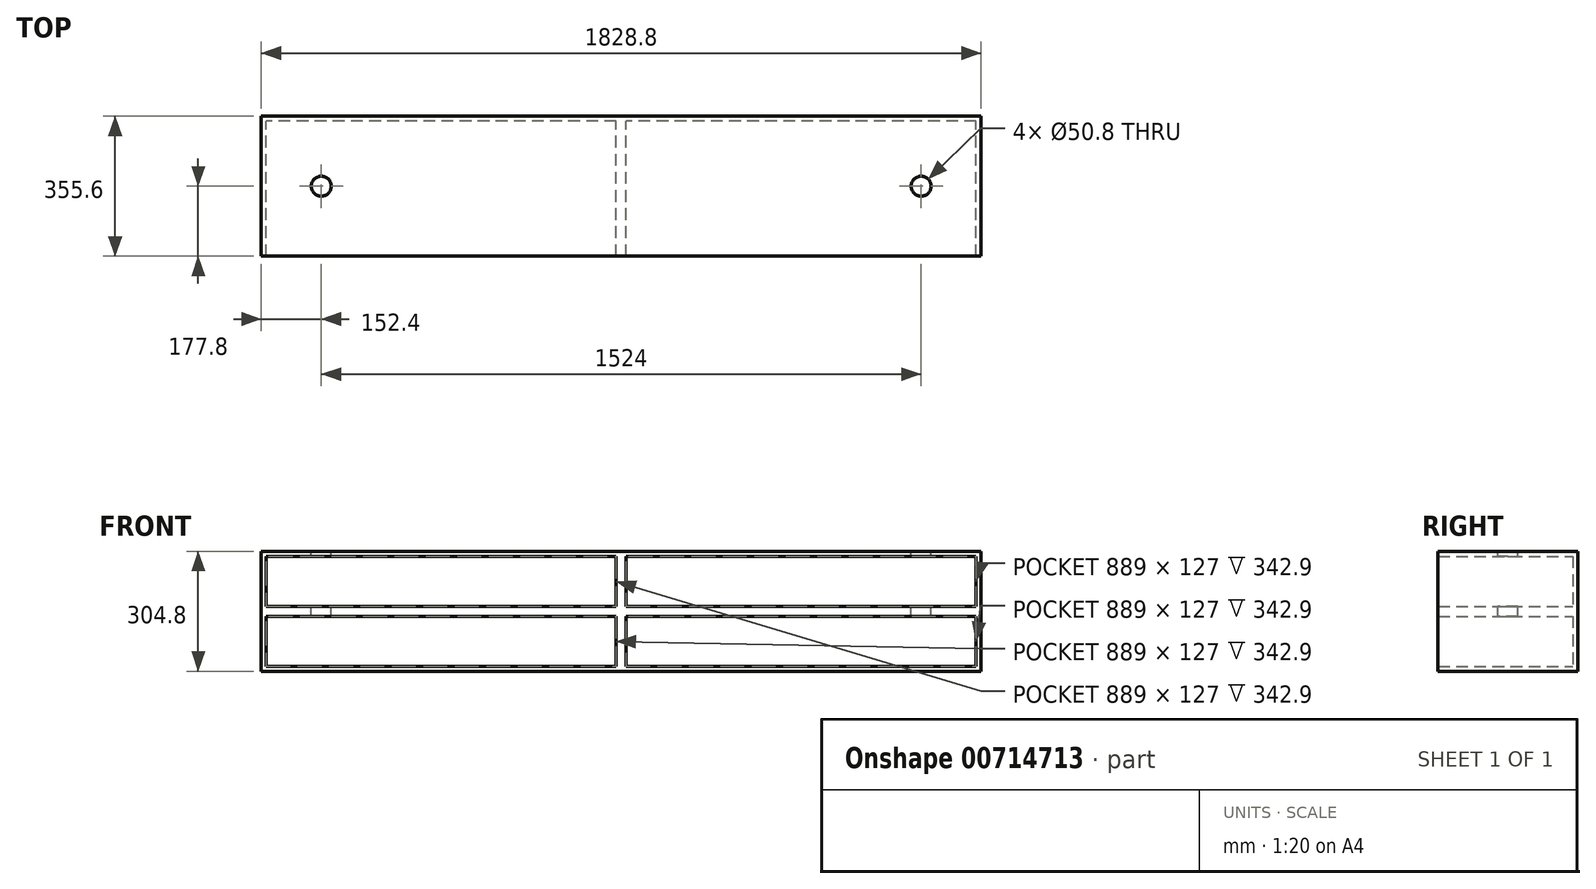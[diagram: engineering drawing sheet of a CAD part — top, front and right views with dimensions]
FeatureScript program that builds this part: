
annotation { "Feature Type Name" : "Feature", "Feature Type Description" : "" }
export const myFeature = defineFeature(function(context is Context, id is Id, definition is map)
    precondition{}
    {
        {
            var Q0;
            Q0=qCreatedBy(makeId("Front.planeOp"),FACE);
            var sketch = newSketch(context, id + "F0", { "sketchPlane" : qUnion([Q0])});
            skLineSegment(sketch, "E0.bottom", {"start": v(914.4, 152.4) * mm, "end": v(-914.4, 152.4) * mm});
            skLineSegment(sketch, "E0.top", {"start": v(914.4, -152.4) * mm, "end": v(-914.4, -152.4) * mm});
            skLineSegment(sketch, "E0.left", {"start": v(914.4, 152.4) * mm, "end": v(914.4, -152.4) * mm});
            skLineSegment(sketch, "E0.right", {"start": v(-914.4, 152.4) * mm, "end": v(-914.4, -152.4) * mm});
            skPoint(sketch, "E0.middle", {"position": v(0, 0) * mm});
            skSolve(sketch);
        }
        {
            var Q0;
            Q0 = qSketchRegion(id + "F0", true);
            extrude(context, id + "F1", {"entities" : qUnion([Q0]), "depth" : 355.6 * mm, "offsetDistance" : 25.4 * mm});
        }
        {
            var Q0;
            Q0=makeQuery(id+"F1.opExtrude","CAP_FACE",FACE,{"disambiguationData":[OSD([sQuery(id+"F0.wireOp",EDGE,"E0.bottom"),sQuery(id+"F0.wireOp",EDGE,"E0.top"),sQuery(id+"F0.wireOp",EDGE,"E0.left"),sQuery(id+"F0.wireOp",EDGE,"E0.right")])],"isStart":false});
            shell(context, id + "F2", {"entities" : qUnion([Q0]), "thickness" : 12.7 * mm});
        }
        {
            var Q0;
            Q0=makeQuery(id+"F2.opShell","OFFSET_FACE",FACE,{"disambiguationData":[OSD([sQuery(id+"F0.wireOp",EDGE,"E0.bottom"),sQuery(id+"F0.wireOp",EDGE,"E0.top"),sQuery(id+"F0.wireOp",EDGE,"E0.left"),sQuery(id+"F0.wireOp",EDGE,"E0.right")])]});
            var sketch = newSketch(context, id + "F3", { "sketchPlane" : qUnion([Q0])});
            skLineSegment(sketch, "E1.bottom", {"start": v(12.7, 139.7) * mm, "end": v(-12.7, 139.7) * mm});
            skLineSegment(sketch, "E1.top", {"start": v(12.7, -139.7) * mm, "end": v(-12.7, -139.7) * mm});
            skLineSegment(sketch, "E1.left", {"start": v(12.7, 139.7) * mm, "end": v(12.7, 12.7) * mm});
            skLineSegment(sketch, "E1.right", {"start": v(-12.7, 139.7) * mm, "end": v(-12.7, 12.7) * mm});
            skPoint(sketch, "E1.middle", {"position": v(0, 0) * mm});
            skLineSegment(sketch, "E2.bottom", {"start": v(901.7, 12.7) * mm, "end": v(12.7, 12.7) * mm});
            skLineSegment(sketch, "E2.top", {"start": v(901.7, -12.7) * mm, "end": v(12.7, -12.7) * mm});
            skLineSegment(sketch, "E2.left", {"start": v(901.7, 12.7) * mm, "end": v(901.7, -12.7) * mm});
            skLineSegment(sketch, "E2.right", {"start": v(-901.7, 12.7) * mm, "end": v(-901.7, -12.7) * mm});
            skLineSegment(sketch, "E3.trimOffspring", {"start": v(-12.7, 12.7) * mm, "end": v(-901.7, 12.7) * mm});
            skLineSegment(sketch, "E4.trimOffspring", {"start": v(-12.7, -12.7) * mm, "end": v(-12.7, -139.7) * mm});
            skLineSegment(sketch, "E5.trimOffspring", {"start": v(12.7, -12.7) * mm, "end": v(12.7, -139.7) * mm});
            skLineSegment(sketch, "E6.trimOffspring", {"start": v(-12.7, -12.7) * mm, "end": v(-901.7, -12.7) * mm});
            skSolve(sketch);
        }
        {
            var Q0;
            Q0 = qSketchRegion(id + "F3", true);
            extrude(context, id + "F4", {"entities" : qUnion([Q0]), "operationType" : NewBodyOperationType.ADD, "depth" : 342.9 * mm, "offsetDistance" : 25.4 * mm});
        }
        {
            var Q0;
            Q0=makeQuery(id+"F1.opExtrude","SWEPT_FACE",FACE,{"disambiguationData":[OSD([sQuery(id+"F0.wireOp",EDGE,"E0.bottom")])]});
            var sketch = newSketch(context, id + "F5", { "sketchPlane" : qUnion([Q0])});
            skCircle(sketch, "E7", {"center": v(762, -177.8) * mm, "radius": 25.4 * mm});
            skCircle(sketch, "E8", {"center": v(-762, -177.8) * mm, "radius": 25.4 * mm});
            skSolve(sketch);
        }
        {
            var Q0;
            Q0=makeQuery(id+"F5.imprint","IMPRINT",FACE,{"disambiguationData":[TD([[makeQuery(id+"F5.imprint","IMPRINT",EDGE,{"derivedFrom":sQuery(id+"F5.wireOp",EDGE,"E8")}),1.0]])]});
            var Q1;
            Q1=makeQuery(id+"F5.imprint","IMPRINT",FACE,{"disambiguationData":[TD([[makeQuery(id+"F5.imprint","IMPRINT",EDGE,{"derivedFrom":sQuery(id+"F5.wireOp",EDGE,"E7")}),1.0]])]});
            extrude(context, id + "F6", {"entities" : qUnion([Q0, Q1]), "operationType" : NewBodyOperationType.REMOVE, "oppositeDirection" : true, "depth" : 190.5 * mm, "offsetDistance" : 25.4 * mm});
        }
    });
